# Revit family: xxxToilet_System-American_Standard-Afwall-Millenium_FloWise-3351.576
name_source: partatom
category: Plumbing Fixtures
units: mm (PartAtom-declared; Revit-internal decimal feet)

## family parameters
Cut with Voids When Loaded = No
Host = Face
OmniClass Number = 23.45.05.21.11.11
OmniClass Title = Water Operated Water Closets
Part Type = Normal
Room Calculation Point = No
Round Connector Dimension = Use Diameter
Shared = Yes

## types (1)
- 3351.576.020
    ADA Compliant = Yes
    ADA Constraint = 15"
    Assembly Code = D2010110
    CW Connection = Yes
    CW Connection Width (4 1/4" - 5 1/4") = 4 1/4"
    CW Connection Width Constraint = 4 1/4"
    CWFU = 5
    Cold Water Connection Diameter = 1"
    Cold Water Connection Height = 11 1/2"
    Default Elevation = 0"
    Description = Afwall® Millennium® Wall-Hung EverClean® Toilet System With Touchless Selectronic® Piston Flush Valve, DF 1.6/1.1 gpf (6.0/4.2 Lpf)
    Finish = Vitreous China-American Standard-020-White
    Finish- Flush Valve = Metal-American Standard-002-Polished Chrome
    Flow Requirement = 25gpm (94.6 L/min.)
    Flush Rate = 1.1 gpf to 1.6 gpf (4.2 Lpf to 6.0 Lpf)
    Flush Valve Specification = https://americanstandard.box.com
    HW Connection = No
    HWFU = 0
    Height = 13 1/8"
    Height- Flush Valve = 16 1/2"
    Length = 26"
    Manufacturer = American Standard
    Material = Vitreous China-American Standard-020-White
    Model = 3351.576.020
    Mounting Height Constraint = 15"
    Mounting Height for ADA (15"-17") = 15"
    Operating Pressure = 25 psi (flowing) - 80 psi (static)
    Product Documentation Link = https://americanstandard.box.com
    Product URL = https://www.americanstandard-us.com
    Revised Date = 01/10/2022
    URL = https://www.americanstandard-us.com
    Vent Connection = No
    WFU = 5
    Waste Connection = Yes
    Waste Connection Diameter = 2 1/8"
    Waste Connection Height = 5 1/4"
    Width = 14"

## geometry (parser evidence)
native form markers: Sweep x2
no freeform markers — native parametric forms only
